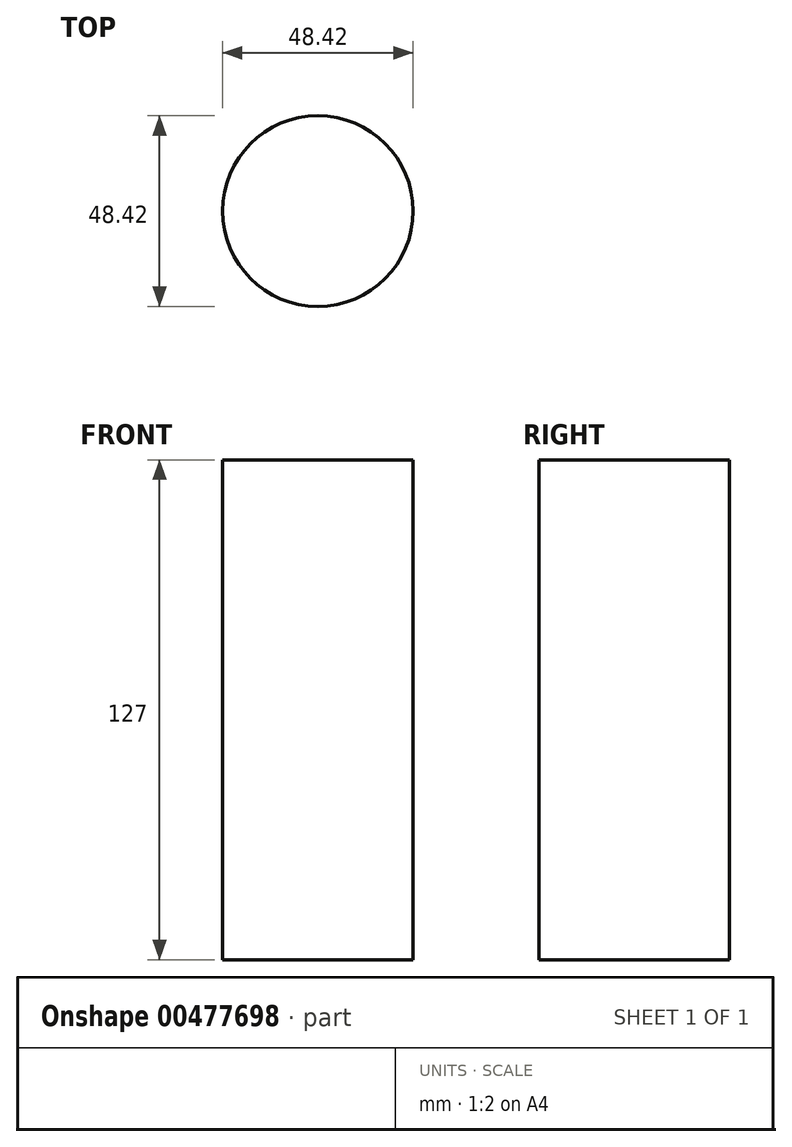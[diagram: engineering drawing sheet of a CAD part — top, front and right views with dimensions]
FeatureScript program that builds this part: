
annotation { "Feature Type Name" : "Feature", "Feature Type Description" : "" }
export const myFeature = defineFeature(function(context is Context, id is Id, definition is map)
    precondition{}
    {
        {
            var Q0;
            Q0=qCreatedBy(makeId("Top.planeOp"),FACE);
            var sketch = newSketch(context, id + "F0", { "sketchPlane" : qUnion([Q0])});
            skCircle(sketch, "E0", {"center": v(0, 0) * mm, "radius": 24.21 * mm});
            skSolve(sketch);
        }
        {
            var Q0;
            Q0 = qSketchRegion(id + "F0", true);
            extrude(context, id + "F1", {"entities" : qUnion([Q0]), "depth" : 127 * mm});
        }
    });
